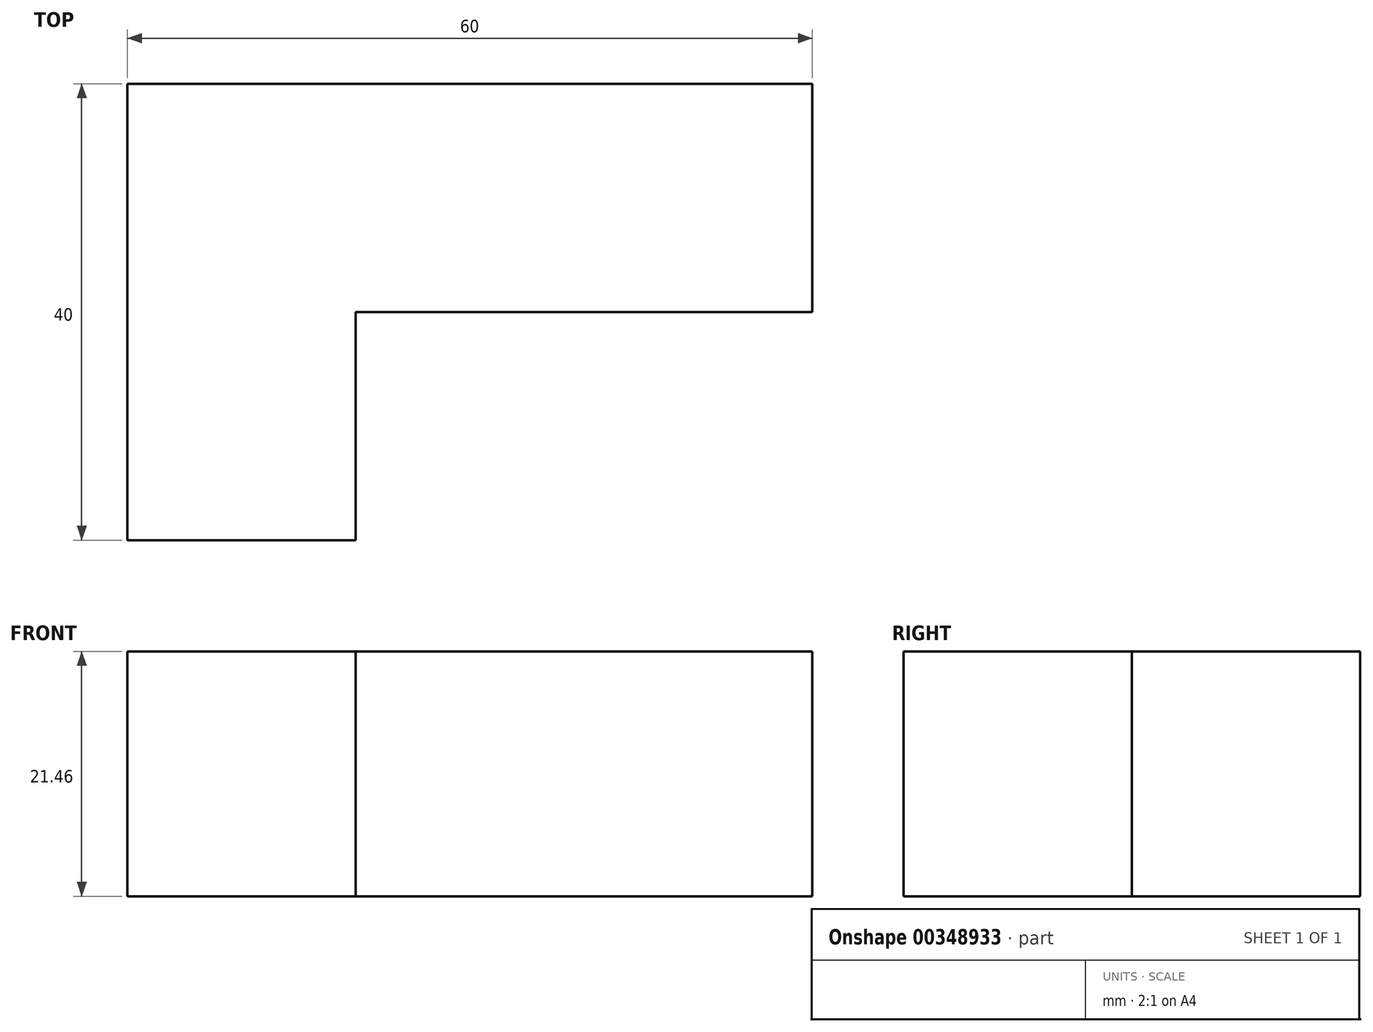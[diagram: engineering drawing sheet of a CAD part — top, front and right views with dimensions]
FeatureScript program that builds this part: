
annotation { "Feature Type Name" : "Feature", "Feature Type Description" : "" }
export const myFeature = defineFeature(function(context is Context, id is Id, definition is map)
    precondition{}
    {
        {
            var Q0;
            Q0=qCreatedBy(makeId("Front.planeOp"),FACE);
            var sketch = newSketch(context, id + "F0", { "sketchPlane" : qUnion([Q0])});
            skLineSegment(sketch, "E0.bottom", {"start": v(-30, 30) * mm, "end": v(30, 30) * mm});
            skLineSegment(sketch, "E0.top", {"start": v(-30, -30) * mm, "end": v(30, -30) * mm});
            skLineSegment(sketch, "E0.left", {"start": v(-30, 30) * mm, "end": v(-30, -30) * mm});
            skLineSegment(sketch, "E0.right", {"start": v(30, 30) * mm, "end": v(30, -30) * mm});
            skPoint(sketch, "E0.middle", {"position": v(0, 0) * mm});
            skLineSegment(sketch, "E1.bottom", {"start": v(-30, 10.73) * mm, "end": v(30, 10.73) * mm});
            skLineSegment(sketch, "E1.top", {"start": v(-30, -10.73) * mm, "end": v(30, -10.73) * mm});
            skLineSegment(sketch, "E1.left", {"start": v(-30, 10.73) * mm, "end": v(-30, -10.73) * mm});
            skLineSegment(sketch, "E1.right", {"start": v(30, 10.73) * mm, "end": v(30, -10.73) * mm});
            skSolve(sketch);
        }
        {
            var Q0;
            Q0=makeQuery(id+"F0.imprint","IMPRINT",FACE,{"disambiguationData":[TD([[makeQuery(id+"F0.imprint","IMPRINT",EDGE,{"derivedFrom":sQuery(id+"F0.wireOp",EDGE,"E1.bottom")}),-1.0]])]});
            extrude(context, id + "F1", {"entities" : qUnion([Q0]), "depth" : 20 * mm});
        }
        {
            var Q0;
            Q0=makeQuery(id+"F1.opExtrude","CAP_FACE",FACE,{"disambiguationData":[OSD([sQuery(id+"F0.wireOp",EDGE,"E1.bottom"),sQuery(id+"F0.wireOp",EDGE,"E1.top"),sQuery(id+"F0.wireOp",EDGE,"E1.left"),sQuery(id+"F0.wireOp",EDGE,"E1.right")])],"isStart":false});
            var sketch = newSketch(context, id + "F2", { "sketchPlane" : qUnion([Q0])});
            skLineSegment(sketch, "E2.bottom", {"start": v(-30, 10.73) * mm, "end": v(-10, 10.73) * mm});
            skLineSegment(sketch, "E2.top", {"start": v(-30, -10.73) * mm, "end": v(-10, -10.73) * mm});
            skLineSegment(sketch, "E2.left", {"start": v(-30, 10.73) * mm, "end": v(-30, -10.73) * mm});
            skLineSegment(sketch, "E2.right", {"start": v(-10, 10.73) * mm, "end": v(-10, -10.73) * mm});
            skSolve(sketch);
        }
        {
            var Q0;
            Q0 = qSketchRegion(id + "F2", true);
            extrude(context, id + "F3", {"entities" : qUnion([Q0]), "operationType" : NewBodyOperationType.ADD, "depth" : 20 * mm});
        }
    });
